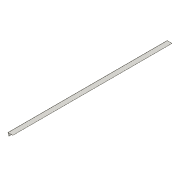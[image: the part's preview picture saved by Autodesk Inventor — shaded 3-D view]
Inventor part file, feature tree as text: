
AUTODESK INVENTOR PART (.ipt)
format: ipt  version: 2018 (Build 220112000, 112)  size: 85,504 bytes
history: native  units: in
note: dims shown in document units (in); Inventor stores cm internally (conversion verified against a paired STEP export)
features: sketch x2, extrude x1
ambient origin geometry x8: Origin, YZ Plane, XZ Plane, XY Plane, X Axis, Y Axis, Z Axis, Center Point
bodies: Solid1 (feature_tree)
feature tree (3):
  extrude  "Extrusion1"  Depth=3.0in
  sketch  "Sketch1"  dims[d0=4.0in d1=3.0in]
  sketch  "Sketch2"  dims[d2=0.0747in d3=0.0747in d4=131.0in d5=0.0in d9=15.0deg d10=1.0in d11=0.0in]
